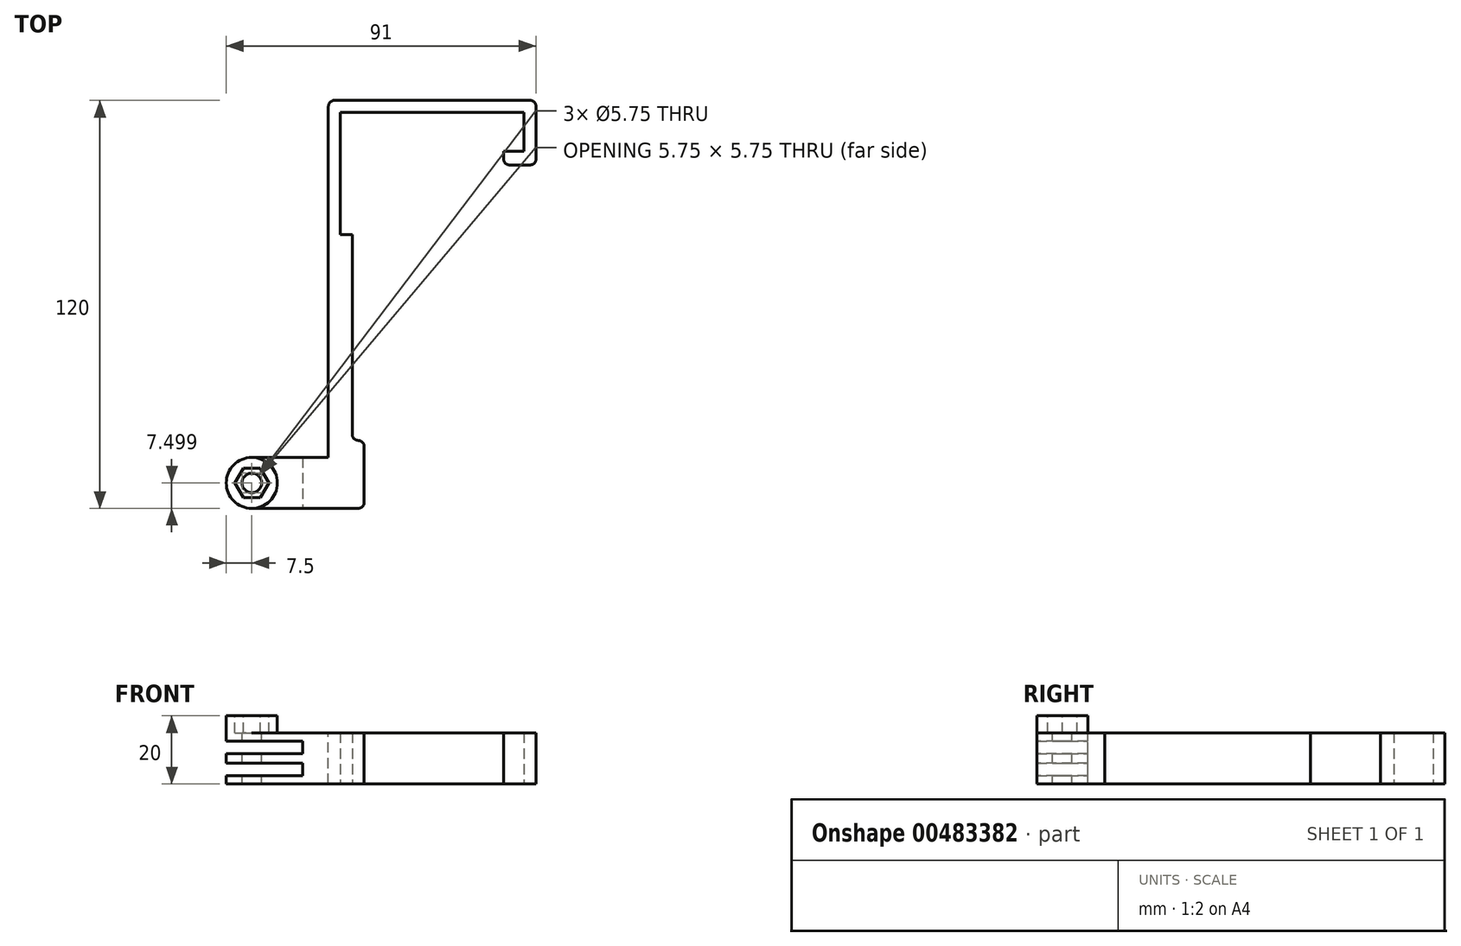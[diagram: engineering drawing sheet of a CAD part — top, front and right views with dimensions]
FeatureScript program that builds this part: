
annotation { "Feature Type Name" : "Feature", "Feature Type Description" : "" }
export const myFeature = defineFeature(function(context is Context, id is Id, definition is map)
    precondition{}
    {
        {
            var Q0;
            Q0=qCreatedBy(makeId("Top.planeOp"),FACE);
            var sketch = newSketch(context, id + "F0", { "sketchPlane" : qUnion([Q0])});
            skLineSegment(sketch, "E0", {"start": v(-30, 28.99) * mm, "end": v(31, 28.99) * mm});
            skLineSegment(sketch, "E1", {"start": v(-26.5, 25.49) * mm, "end": v(27.5, 25.49) * mm});
            skLineSegment(sketch, "E2", {"start": v(27.5, 25.49) * mm, "end": v(27.5, 13.99) * mm});
            skLineSegment(sketch, "E3", {"start": v(-26.5, 25.49) * mm, "end": v(-26.5, -41.01) * mm});
            skLineSegment(sketch, "E4", {"start": v(27.5, 13.99) * mm, "end": v(21.5, 13.99) * mm});
            skLineSegment(sketch, "E5", {"start": v(21.5, 13.99) * mm, "end": v(21.5, 9.99) * mm});
            skLineSegment(sketch, "E6", {"start": v(21.5, 9.99) * mm, "end": v(31, 9.99) * mm});
            skLineSegment(sketch, "E7", {"start": v(31, 28.99) * mm, "end": v(31, 9.99) * mm});
            skLineSegment(sketch, "E8", {"start": v(-26.5, -41.01) * mm, "end": v(-19.5, -41.01) * mm});
            skLineSegment(sketch, "E9", {"start": v(-19.5, -41.01) * mm, "end": v(-19.5, -91.01) * mm});
            skLineSegment(sketch, "E10", {"start": v(-19.5, -91.01) * mm, "end": v(-30, -91.01) * mm});
            skLineSegment(sketch, "E11", {"start": v(-30, 28.99) * mm, "end": v(-30, -91.01) * mm});
            skLineSegment(sketch, "E12", {"start": v(-26.5, -41.01) * mm, "end": v(-26.5, -51.01) * mm});
            skLineSegment(sketch, "E13", {"start": v(-26.5, -51.01) * mm, "end": v(-19.5, -51.01) * mm});
            skLineSegment(sketch, "E14", {"start": v(-26.5, -51.01) * mm, "end": v(-26.5, -71.01) * mm});
            skLineSegment(sketch, "E15", {"start": v(-26.5, -71.01) * mm, "end": v(-19.5, -71.01) * mm});
            skLineSegment(sketch, "E16", {"start": v(-23, -51.01) * mm, "end": v(-23, -71.01) * mm});
            skLineSegment(sketch, "E17", {"start": v(-23, -41.01) * mm, "end": v(-23, -71.01) * mm});
            skSolve(sketch);
        }
        {
            var Q0;
            {var subQ0=sQuery(id+"F0.wireOp",EDGE,"E12");Q0=makeQuery(id+"F0.imprint","IMPRINT",FACE,{"disambiguationData":[TD([[makeQuery(id+"F0.imprint","IMPRINT",EDGE,{"derivedFrom":subQ0}),1.0]])]});}
            var Q1;
            Q1=makeQuery(id+"F0.imprint","IMPRINT",FACE,{"disambiguationData":[TD([[makeQuery(id+"F0.imprint","IMPRINT",EDGE,{"derivedFrom":sQuery(id+"F0.wireOp",EDGE,"E0")}),-1.0]])]});
            var Q2;
            {var subQ0=sQuery(id+"F0.wireOp",EDGE,"E14");Q2=makeQuery(id+"F0.imprint","IMPRINT",FACE,{"disambiguationData":[TD([[makeQuery(id+"F0.imprint","IMPRINT",EDGE,{"derivedFrom":subQ0}),1.0]])]});}
            extrude(context, id + "F1", {"entities" : qUnion([Q0, Q1, Q2]), "depth" : 15 * mm});
        }
        {
            var Q0;
            Q0=makeQuery(id+"F1.opExtrude","SWEPT_FACE",FACE,{"disambiguationData":[OSD([sQuery(id+"F0.wireOp",EDGE,"E11")])]});
            var sketch = newSketch(context, id + "F2", { "sketchPlane" : qUnion([Q0])});
            skLineSegment(sketch, "E18.bottom", {"start": v(91.01, 0) * mm, "end": v(76.01, 0) * mm});
            skLineSegment(sketch, "E18.top", {"start": v(91.01, 15) * mm, "end": v(76.01, 15) * mm});
            skLineSegment(sketch, "E18.left", {"start": v(91.01, 0) * mm, "end": v(91.01, 15) * mm});
            skLineSegment(sketch, "E18.right", {"start": v(76.01, 0) * mm, "end": v(76.01, 15) * mm});
            skSolve(sketch);
        }
        {
            var Q0;
            Q0=makeQuery(id+"F2.imprint","IMPRINT",FACE,{"disambiguationData":[TD([[makeQuery(id+"F2.imprint","IMPRINT",EDGE,{"derivedFrom":sQuery(id+"F2.wireOp",EDGE,"E18.bottom")}),1.0]])]});
            extrude(context, id + "F3", {"entities" : qUnion([Q0]), "operationType" : NewBodyOperationType.ADD, "depth" : 30 * mm});
        }
        {
            var Q0;
            Q0=makeQuery(id+"F3.boolean.opBoolean","MERGE",FACE,{"derivedFrom":[makeQuery(id+"F1.opExtrude","CAP_FACE",FACE,{"disambiguationData":[OSD([sQuery(id+"F0.wireOp",EDGE,"E0"),sQuery(id+"F0.wireOp",EDGE,"E1"),sQuery(id+"F0.wireOp",EDGE,"E2"),sQuery(id+"F0.wireOp",EDGE,"E3"),sQuery(id+"F0.wireOp",EDGE,"E4"),sQuery(id+"F0.wireOp",EDGE,"E5"),sQuery(id+"F0.wireOp",EDGE,"E6"),sQuery(id+"F0.wireOp",EDGE,"E7"),sQuery(id+"F0.wireOp",EDGE,"E8"),sQuery(id+"F0.wireOp",EDGE,"E9"),sQuery(id+"F0.wireOp",EDGE,"E10"),sQuery(id+"F0.wireOp",EDGE,"E11"),sQuery(id+"F0.wireOp",EDGE,"E13"),sQuery(id+"F0.wireOp",EDGE,"E15"),sQuery(id+"F0.wireOp",EDGE,"E16")])],"isStart":false}),makeQuery(id+"F3.opExtrude","SWEPT_FACE",FACE,{"disambiguationData":[OSD([sQuery(id+"F2.wireOp",EDGE,"E18.top")])]})]});
            var sketch = newSketch(context, id + "F4", { "sketchPlane" : qUnion([Q0])});
            skLineSegment(sketch, "E19", {"start": v(-30, -76.01) * mm, "end": v(-30, -91.01) * mm});
            skLineSegment(sketch, "E20", {"start": v(-60, -83.51) * mm, "end": v(-52.5, -83.51) * mm});
            skCircle(sketch, "E21", {"center": v(-52.5, -83.51) * mm, "radius": 2.88 * mm});
            skCircle(sketch, "E22", {"center": v(-52.5, -83.51) * mm, "radius": 7.5 * mm});
            skSolve(sketch);
        }
        {
            var Q0;
            {var subQ0=sQuery(id+"F4.wireOp",EDGE,"E22");var subQ1=sQuery(id+"F2.wireOp",EDGE,"E18.top");var subQ2=makeQuery(id+"F3.opExtrude","CAP_EDGE",EDGE,{"disambiguationData":[OSD([subQ1])],"isStart":false});var subQ3=makeQuery(id+"F4.imprint","INTERSECT",VERTEX,{"derivedFrom":[subQ2,subQ0]});Q0=makeQuery(id+"F4.imprint","IMPRINT",FACE,{"disambiguationData":[TD([[makeQuery(id+"F4.imprint","IMPRINT",EDGE,{"disambiguationData":[TD([[subQ3,1.0]])],"derivedFrom":subQ0}),-1.0]])]});}
            var Q1;
            {var subQ0=sQuery(id+"F4.wireOp",EDGE,"E22");var subQ1=sQuery(id+"F2.wireOp",EDGE,"E18.top");var subQ2=makeQuery(id+"F3.opExtrude","CAP_EDGE",EDGE,{"disambiguationData":[OSD([subQ1])],"isStart":false});var subQ3=makeQuery(id+"F4.imprint","INTERSECT",VERTEX,{"derivedFrom":[subQ2,subQ0]});Q1=makeQuery(id+"F4.imprint","IMPRINT",FACE,{"disambiguationData":[TD([[makeQuery(id+"F4.imprint","IMPRINT",EDGE,{"disambiguationData":[TD([[subQ3,-1.0]])],"derivedFrom":subQ0}),-1.0]])]});}
            extrude(context, id + "F5", {"entities" : qUnion([Q0, Q1]), "operationType" : NewBodyOperationType.REMOVE, "oppositeDirection" : true, "depth" : 25 * mm});
        }
        {
            var Q0;
            Q0=makeQuery(id+"F4.imprint","IMPRINT",FACE,{"disambiguationData":[TD([[makeQuery(id+"F4.imprint","IMPRINT",EDGE,{"derivedFrom":sQuery(id+"F4.wireOp",EDGE,"E21")}),-1.0]])]});
            extrude(context, id + "F6", {"entities" : qUnion([Q0]), "operationType" : NewBodyOperationType.ADD, "depth" : 5 * mm});
        }
        {
            var Q0;
            Q0=makeQuery(id+"F6.opExtrude","CAP_FACE",FACE,{"disambiguationData":[OSD([sQuery(id+"F4.wireOp",EDGE,"E21"),sQuery(id+"F4.wireOp",EDGE,"E22")])],"isStart":false});
            var sketch = newSketch(context, id + "F7", { "sketchPlane" : qUnion([Q0])});
            skCircle(sketch, "E23.cCircle", {"center": v(-52.5, -83.51) * mm, "radius": 4.33 * mm, "construction": true});
            skLineSegment(sketch, "E23.0", {"start": v(-55, -79.18) * mm, "end": v(-50, -79.18) * mm});
            skLineSegment(sketch, "E23.1", {"start": v(-50, -79.18) * mm, "end": v(-47.5, -83.51) * mm});
            skLineSegment(sketch, "E23.2", {"start": v(-47.5, -83.51) * mm, "end": v(-50, -87.84) * mm});
            skLineSegment(sketch, "E23.3", {"start": v(-50, -87.84) * mm, "end": v(-55, -87.84) * mm});
            skLineSegment(sketch, "E23.4", {"start": v(-55, -87.84) * mm, "end": v(-57.5, -83.51) * mm});
            skLineSegment(sketch, "E23.5", {"start": v(-57.5, -83.51) * mm, "end": v(-55, -79.18) * mm});
            skPoint(sketch, "E23.0.midPoint", {"position": v(-52.5, -79.18) * mm});
            skSolve(sketch);
        }
        {
            var Q0;
            Q0=makeQuery(id+"F7.imprint","IMPRINT",FACE,{"disambiguationData":[TD([[makeQuery(id+"F7.imprint","IMPRINT",EDGE,{"derivedFrom":sQuery(id+"F7.wireOp",EDGE,"E23.0")}),-1.0]])]});
            extrude(context, id + "F8", {"entities" : qUnion([Q0]), "operationType" : NewBodyOperationType.REMOVE, "oppositeDirection" : true, "depth" : 5 * mm});
        }
        {
            var Q0;
            Q0=makeQuery(id+"F4.imprint","IMPRINT",FACE,{"disambiguationData":[TD([[makeQuery(id+"F4.imprint","IMPRINT",EDGE,{"derivedFrom":sQuery(id+"F4.wireOp",EDGE,"E21")}),1.0]])]});
            extrude(context, id + "F9", {"entities" : qUnion([Q0]), "operationType" : NewBodyOperationType.REMOVE, "oppositeDirection" : true, "depth" : 25 * mm});
        }
        {
            var Q0;
            Q0=makeQuery(id+"F3.boolean.opBoolean","MERGE",FACE,{"derivedFrom":[makeQuery(id+"F1.opExtrude","SWEPT_FACE",FACE,{"disambiguationData":[OSD([sQuery(id+"F0.wireOp",EDGE,"E10")])]}),makeQuery(id+"F3.opExtrude","SWEPT_FACE",FACE,{"disambiguationData":[OSD([sQuery(id+"F2.wireOp",EDGE,"E18.left")])]})]});
            var sketch = newSketch(context, id + "F10", { "sketchPlane" : qUnion([Q0])});
            skLineSegment(sketch, "E24.bottom", {"start": v(-45, 15) * mm, "end": v(-60, 15) * mm});
            skLineSegment(sketch, "E24.top", {"start": v(-45, 0) * mm, "end": v(-60, 0) * mm});
            skLineSegment(sketch, "E24.left", {"start": v(-45, 15) * mm, "end": v(-45, 0) * mm});
            skLineSegment(sketch, "E24.right", {"start": v(-60, 15) * mm, "end": v(-60, 0) * mm});
            skLineSegment(sketch, "E25", {"start": v(-60, 12.6) * mm, "end": v(-45, 12.6) * mm});
            skLineSegment(sketch, "E26.bottom", {"start": v(-60, 8.9) * mm, "end": v(-45, 8.9) * mm});
            skLineSegment(sketch, "E26.top", {"start": v(-60, 6.1) * mm, "end": v(-45, 6.1) * mm});
            skLineSegment(sketch, "E26.left", {"start": v(-60, 8.9) * mm, "end": v(-60, 6.1) * mm});
            skLineSegment(sketch, "E26.right", {"start": v(-45, 8.9) * mm, "end": v(-45, 6.1) * mm});
            skLineSegment(sketch, "E27", {"start": v(-60, 2.4) * mm, "end": v(-45, 2.4) * mm});
            skLineSegment(sketch, "E28", {"start": v(-52.5, 15) * mm, "end": v(-52.5, 0) * mm});
            skLineSegment(sketch, "E29.MirrorCS", {"start": v(-37.5, 12.6) * mm, "end": v(-45, 12.6) * mm});
            skLineSegment(sketch, "E30.MirrorCS", {"start": v(-45, 15) * mm, "end": v(-37.5, 15) * mm});
            skLineSegment(sketch, "E31.MirrorCS", {"start": v(-37.5, 8.9) * mm, "end": v(-45, 8.9) * mm});
            skLineSegment(sketch, "E32.MirrorCS", {"start": v(-37.5, 2.4) * mm, "end": v(-45, 2.4) * mm});
            skLineSegment(sketch, "E33.MirrorCS", {"start": v(-45, 0) * mm, "end": v(-37.5, 0) * mm});
            skLineSegment(sketch, "E34.MirrorCS", {"start": v(-37.5, 15) * mm, "end": v(-37.5, 0) * mm});
            skPoint(sketch, "E35.orphan", {"position": v(-30, 15) * mm});
            skPoint(sketch, "E36.orphan", {"position": v(-30, 12.6) * mm});
            skPoint(sketch, "E37.orphan", {"position": v(-30, 8.9) * mm});
            skPoint(sketch, "E38.orphan", {"position": v(-30, 6.1) * mm});
            skPoint(sketch, "E39.MirrorCS.end.orphan", {"position": v(-45, 6.1) * mm});
            skPoint(sketch, "E40.orphan", {"position": v(-30, 2.4) * mm});
            skPoint(sketch, "E41.orphan", {"position": v(-30, 0) * mm});
            skLineSegment(sketch, "E42", {"start": v(-45, 6.1) * mm, "end": v(-37.5, 6.1) * mm});
            skPoint(sketch, "E43.start.orphan", {"position": v(-60, 7.5) * mm});
            skSolve(sketch);
        }
        {
            var Q0;
            {var subQ0=sQuery(id+"F10.wireOp",EDGE,"E25");var subQ1=sQuery(id+"F10.wireOp",EDGE,"E24.right");var subQ2=makeQuery(id+"F10.imprint","INTERSECT",VERTEX,{"derivedFrom":[subQ1,subQ0]});Q0=makeQuery(id+"F10.imprint","IMPRINT",FACE,{"disambiguationData":[TD([[makeQuery(id+"F10.imprint","IMPRINT",EDGE,{"disambiguationData":[TD([[subQ2,-1.0]])],"derivedFrom":subQ1}),1.0]])]});}
            var Q1;
            {var subQ0=sQuery(id+"F10.wireOp",EDGE,"E25");var subQ1=sQuery(id+"F10.wireOp",EDGE,"E24.left");var subQ2=makeQuery(id+"F10.imprint","INTERSECT",VERTEX,{"derivedFrom":[subQ1,subQ0]});Q1=makeQuery(id+"F10.imprint","IMPRINT",FACE,{"disambiguationData":[TD([[makeQuery(id+"F10.imprint","IMPRINT",EDGE,{"disambiguationData":[TD([[subQ2,-1.0]])],"derivedFrom":subQ1}),-1.0]])]});}
            var Q2;
            {var subQ1=sQuery(id+"F10.wireOp",EDGE,"E24.right");var subQ3=sQuery(id+"F10.wireOp",EDGE,"E27");var subQ4=makeQuery(id+"F10.imprint","INTERSECT",VERTEX,{"derivedFrom":[subQ1,subQ3]});Q2=makeQuery(id+"F10.imprint","IMPRINT",FACE,{"disambiguationData":[TD([[makeQuery(id+"F10.imprint","IMPRINT",EDGE,{"disambiguationData":[TD([[subQ4,1.0]])],"derivedFrom":subQ1}),1.0]])]});}
            var Q3;
            {var subQ1=sQuery(id+"F10.wireOp",EDGE,"E24.left");var subQ3=sQuery(id+"F10.wireOp",EDGE,"E27");var subQ4=makeQuery(id+"F10.imprint","INTERSECT",VERTEX,{"derivedFrom":[subQ1,subQ3]});Q3=makeQuery(id+"F10.imprint","IMPRINT",FACE,{"disambiguationData":[TD([[makeQuery(id+"F10.imprint","IMPRINT",EDGE,{"disambiguationData":[TD([[subQ4,1.0]])],"derivedFrom":subQ1}),-1.0]])]});}
            var Q4;
            {var subQ0=sQuery(id+"F10.wireOp",EDGE,"E29.MirrorCS");Q4=makeQuery(id+"F10.imprint","IMPRINT",FACE,{"disambiguationData":[TD([[makeQuery(id+"F10.imprint","IMPRINT",EDGE,{"derivedFrom":subQ0}),1.0]])]});}
            var Q5;
            {var subQ2=sQuery(id+"F10.wireOp",EDGE,"E32.MirrorCS");Q5=makeQuery(id+"F10.imprint","IMPRINT",FACE,{"disambiguationData":[TD([[makeQuery(id+"F10.imprint","IMPRINT",EDGE,{"derivedFrom":subQ2}),-1.0]])]});}
            extrude(context, id + "F11", {"entities" : qUnion([Q0, Q1, Q2, Q3, Q4, Q5]), "operationType" : NewBodyOperationType.REMOVE, "oppositeDirection" : true, "depth" : 25 * mm});
        }
        {
            var Q0;
            Q0=makeQuery(id+"F1.opExtrude","SWEPT_FACE",FACE,{"disambiguationData":[OSD([sQuery(id+"F0.wireOp",EDGE,"E3")])]});
            var sketch = newSketch(context, id + "F12", { "sketchPlane" : qUnion([Q0])});
            skLineSegment(sketch, "E44.bottom", {"start": v(-41.01, 15) * mm, "end": v(-10.51, 15) * mm});
            skLineSegment(sketch, "E44.top", {"start": v(-41.01, 0) * mm, "end": v(-10.51, 0) * mm});
            skLineSegment(sketch, "E44.left", {"start": v(-41.01, 15) * mm, "end": v(-41.01, 0) * mm});
            skLineSegment(sketch, "E44.right", {"start": v(-10.51, 15) * mm, "end": v(-10.51, 0) * mm});
            skSolve(sketch);
        }
        {
            var Q0;
            Q0=makeQuery(id+"F12.imprint","IMPRINT",FACE,{"disambiguationData":[TD([[makeQuery(id+"F12.imprint","IMPRINT",EDGE,{"derivedFrom":sQuery(id+"F12.wireOp",EDGE,"E44.bottom")}),1.0]])]});
            extrude(context, id + "F13", {"entities" : qUnion([Q0]), "operationType" : NewBodyOperationType.ADD, "depth" : 3.5 * mm});
        }
        {
            var Q0;
            Q0=makeQuery(id+"F1.opExtrude","SWEPT_EDGE",EDGE,{"disambiguationData":[OSD([sQuery(id+"F0.wireOp",EDGE,"E15"),sQuery(id+"F0.wireOp",EDGE,"E17")])]});
            var Q1;
            Q1=makeQuery(id+"F1.opExtrude","SWEPT_EDGE",EDGE,{"disambiguationData":[OSD([sQuery(id+"F0.wireOp",EDGE,"E9"),sQuery(id+"F0.wireOp",EDGE,"E15")])]});
            var Q2;
            Q2=makeQuery(id+"F1.opExtrude","SWEPT_EDGE",EDGE,{"disambiguationData":[OSD([sQuery(id+"F0.wireOp",EDGE,"E9"),sQuery(id+"F0.wireOp",EDGE,"E10")])]});
            var Q3;
            Q3=makeQuery(id+"F3.opExtrude","CAP_EDGE",EDGE,{"disambiguationData":[OSD([sQuery(id+"F2.wireOp",EDGE,"E18.right")])],"isStart":true});
            var Q4;
            Q4=makeQuery(id+"F1.opExtrude","SWEPT_EDGE",EDGE,{"disambiguationData":[OSD([sQuery(id+"F0.wireOp",EDGE,"E0"),sQuery(id+"F0.wireOp",EDGE,"E11")])]});
            var Q5;
            Q5=makeQuery(id+"F1.opExtrude","SWEPT_EDGE",EDGE,{"disambiguationData":[OSD([sQuery(id+"F0.wireOp",EDGE,"E0"),sQuery(id+"F0.wireOp",EDGE,"E7")])]});
            var Q6;
            Q6=makeQuery(id+"F1.opExtrude","SWEPT_EDGE",EDGE,{"disambiguationData":[OSD([sQuery(id+"F0.wireOp",EDGE,"E6"),sQuery(id+"F0.wireOp",EDGE,"E7")])]});
            var Q7;
            Q7=makeQuery(id+"F1.opExtrude","SWEPT_EDGE",EDGE,{"disambiguationData":[OSD([sQuery(id+"F0.wireOp",EDGE,"E5"),sQuery(id+"F0.wireOp",EDGE,"E6")])]});
            fillet(context, id + "F14", {"entities" : qUnion([Q0, Q1, Q2, Q3, Q4, Q5, Q6, Q7]), "radius" : 1.75 * mm, "tangentPropagation" : true, "allowEdgeOverflow" : false});
        }
    });
